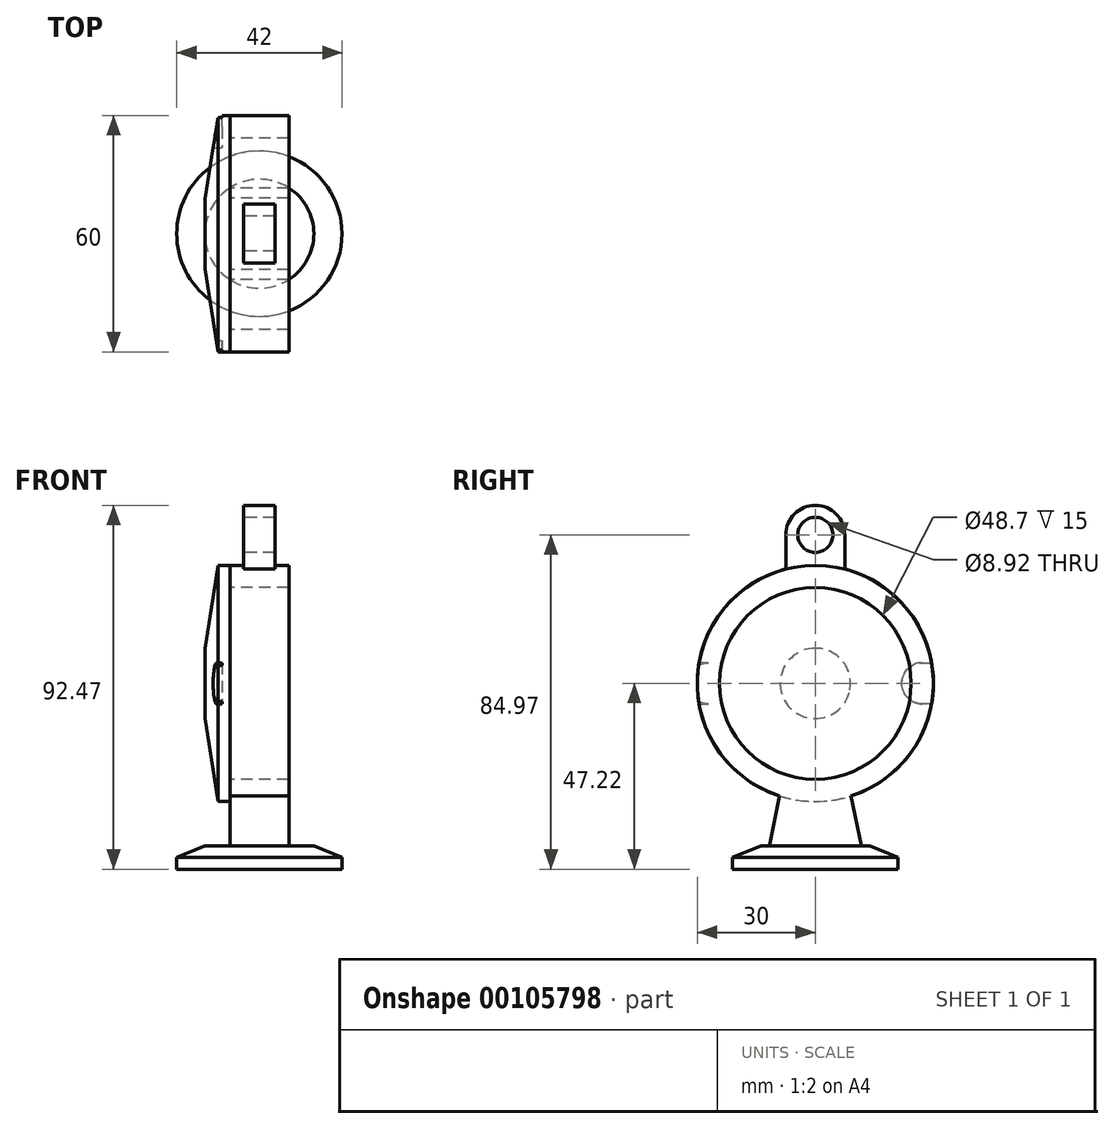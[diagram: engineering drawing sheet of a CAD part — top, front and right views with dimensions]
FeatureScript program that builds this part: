
annotation { "Feature Type Name" : "Feature", "Feature Type Description" : "" }
export const myFeature = defineFeature(function(context is Context, id is Id, definition is map)
    precondition{}
    {
        {
            var Q0;
            Q0=qCreatedBy(makeId("Right.planeOp"),FACE);
            var sketch = newSketch(context, id + "F0", { "sketchPlane" : qUnion([Q0])});
            skCircle(sketch, "E0", {"center": v(0, 0) * mm, "radius": 30 * mm});
            skArc(sketch, "E1", {"start": v(7.5, 37.75) * mm, "mid": v(0, 45.25) * mm, "end": v(-7.5, 37.75) * mm});
            skLineSegment(sketch, "E2", {"start": v(7.5, 37.75) * mm, "end": v(7.5, 29.05) * mm});
            skLineSegment(sketch, "E3", {"start": v(-7.5, 37.75) * mm, "end": v(-7.5, 29.05) * mm});
            skCircle(sketch, "E4", {"center": v(0, 0) * mm, "radius": 24.35 * mm});
            skCircle(sketch, "E5", {"center": v(0, 37.75) * mm, "radius": 4.46 * mm});
            skLineSegment(sketch, "E6", {"start": v(0, 46.89) * mm, "end": v(0, -52.68) * mm, "construction": true});
            skLineSegment(sketch, "E7", {"start": v(9.09, -28.6) * mm, "end": v(11.66, -41.22) * mm});
            skLineSegment(sketch, "E8.MirrorCS", {"start": v(-9.09, -28.6) * mm, "end": v(-11.66, -41.22) * mm});
            skLineSegment(sketch, "E9", {"start": v(11.66, -41.22) * mm, "end": v(-11.66, -41.22) * mm});
            skSolve(sketch);
        }
        {
            var Q0;
            Q0=makeQuery(id+"F0.imprint","IMPRINT",FACE,{"disambiguationData":[TD([[makeQuery(id+"F0.imprint","IMPRINT",EDGE,{"derivedFrom":sQuery(id+"F0.wireOp",EDGE,"E4")}),-1.0]])]});
            var Q1;
            {var subQ0=sQuery(id+"F0.wireOp",EDGE,"E7");Q1=makeQuery(id+"F0.imprint","IMPRINT",FACE,{"disambiguationData":[TD([[makeQuery(id+"F0.imprint","IMPRINT",EDGE,{"derivedFrom":subQ0}),-1.0]])]});}
            extrude(context, id + "F1", {"entities" : qUnion([Q0, Q1]), "endBound" : BoundingType.SYMMETRIC, "depth" : 15 * mm});
        }
        {
            var Q0;
            Q0=makeQuery(id+"F0.imprint","IMPRINT",FACE,{"disambiguationData":[TD([[makeQuery(id+"F0.imprint","IMPRINT",EDGE,{"derivedFrom":sQuery(id+"F0.wireOp",EDGE,"E1")}),1.0]])]});
            extrude(context, id + "F2", {"entities" : qUnion([Q0]), "operationType" : NewBodyOperationType.ADD, "endBound" : BoundingType.SYMMETRIC, "depth" : 8 * mm});
        }
        {
            var Q0;
            Q0=makeQuery(id+"F1.opExtrude","CAP_FACE",FACE,{"disambiguationData":[OSD([sQuery(id+"F0.wireOp",EDGE,"E0"),sQuery(id+"F0.wireOp",EDGE,"E4")])],"isStart":true});
            var sketch = newSketch(context, id + "F3", { "sketchPlane" : qUnion([Q0])});
            skLineSegment(sketch, "E10", {"start": v(0, -30) * mm, "end": v(0, 0) * mm});
            skSolve(sketch);
        }
        {
            var Q0;
            Q0=makeQuery(id+"F1.opExtrude","SWEPT_FACE",FACE,{"disambiguationData":[OSD([sQuery(id+"F0.wireOp",EDGE,"E9")])]});
            var sketch = newSketch(context, id + "F4", { "sketchPlane" : qUnion([Q0])});
            skCircle(sketch, "E11", {"center": v(0, 0) * mm, "radius": 13.86 * mm, "construction": true});
            skSolve(sketch);
        }
        {
            var Q0;
            Q0=qCreatedBy(makeId("Front.planeOp"),FACE);
            var sketch = newSketch(context, id + "F5", { "sketchPlane" : qUnion([Q0])});
            skLineSegment(sketch, "E12", {"start": v(-10.5, -30) * mm, "end": v(-13.75, -8.94) * mm});
            skLineSegment(sketch, "E13", {"start": v(-13.75, -8.94) * mm, "end": v(-13.75, 0) * mm});
            skLineSegment(sketch, "E14", {"start": v(-13.75, 0) * mm, "end": v(-7.5, 0) * mm});
            skLineSegment(sketch, "E15", {"start": v(-10.5, -30) * mm, "end": v(-7.5, -30) * mm});
            skLineSegment(sketch, "E16", {"start": v(-7.5, 0) * mm, "end": v(-7.5, -30) * mm});
            skLineSegment(sketch, "E17", {"start": v(-13.84, -41.22) * mm, "end": v(-21, -44.22) * mm});
            skLineSegment(sketch, "E18", {"start": v(-21, -44.22) * mm, "end": v(-21, -47.22) * mm});
            skLineSegment(sketch, "E19", {"start": v(-21, -47.22) * mm, "end": v(0, -47.22) * mm});
            skLineSegment(sketch, "E20", {"start": v(0, -47.22) * mm, "end": v(0, -41.22) * mm});
            skLineSegment(sketch, "E21", {"start": v(0, -41.22) * mm, "end": v(-13.84, -41.22) * mm});
            skSolve(sketch);
        }
        {
            var Q0;
            Q0=makeQuery(id+"F5.imprint","IMPRINT",FACE,{"disambiguationData":[TD([[makeQuery(id+"F5.imprint","IMPRINT",EDGE,{"derivedFrom":sQuery(id+"F5.wireOp",EDGE,"E12")}),-1.0]])]});
            var Q1;
            Q1=sQuery(id+"F5.wireOp",EDGE,"E14");
            revolve(context, id + "F6", {"entities" : qUnion([Q0]), "axis" : qUnion([Q1]), "revolveType" : RevolveType.FULL});
        }
        {
            var Q0;
            Q0=makeQuery(id+"F3.imprint","IMPRINT",FACE,{"disambiguationData":[TD([[makeQuery(id+"F3.imprint","IMPRINT",EDGE,{"derivedFrom":makeQuery(id+"F1.opExtrude","CAP_EDGE",EDGE,{"disambiguationData":[OSD([sQuery(id+"F0.wireOp",EDGE,"E0")])],"isStart":true})}),-1.0]])]});
            cPlane(context, id + "F7", {"entities" : qUnion([Q0]), "cplaneType" : CPlaneType.OFFSET, "offset" : 2 * mm, "width" : 150 * mm, "height" : 150 * mm});
        }
        {
            var Q0;
            Q0=qCreatedBy(id+"F7.planeOp",FACE);
            var sketch = newSketch(context, id + "F8", { "sketchPlane" : qUnion([Q0])});
            skLineSegment(sketch, "E22", {"start": v(-50.5, 0) * mm, "end": v(44.8, 0) * mm, "construction": true});
            skCircle(sketch, "E23", {"center": v(-27.18, 0) * mm, "radius": 2.82 * mm, "construction": true});
            skCircle(sketch, "E24", {"center": v(-27.18, 0) * mm, "radius": 5.24 * mm});
            skCircle(sketch, "E25.MirrorC", {"center": v(27.18, 0) * mm, "radius": 5.24 * mm});
            skCircle(sketch, "E26.MirrorC", {"center": v(27.18, 0) * mm, "radius": 2.82 * mm, "construction": true});
            skLineSegment(sketch, "E27", {"start": v(-27.18, 5.24) * mm, "end": v(-34.89, 5.24) * mm});
            skLineSegment(sketch, "E28", {"start": v(-34.89, 5.24) * mm, "end": v(-34.89, -5.24) * mm});
            skLineSegment(sketch, "E29", {"start": v(-34.89, -5.24) * mm, "end": v(-27.18, -5.24) * mm});
            skLineSegment(sketch, "E30.MirrorCS", {"start": v(27.18, 5.24) * mm, "end": v(34.89, 5.24) * mm});
            skLineSegment(sketch, "E31.MirrorCS", {"start": v(34.89, 5.24) * mm, "end": v(34.89, -5.24) * mm});
            skLineSegment(sketch, "E32.MirrorCS", {"start": v(34.89, -5.24) * mm, "end": v(27.18, -5.24) * mm});
            skSolve(sketch);
        }
        {
            var Q0;
            Q0=makeQuery(id+"F8.imprint","IMPRINT",FACE,{"disambiguationData":[TD([[makeQuery(id+"F8.imprint","IMPRINT",EDGE,{"derivedFrom":sQuery(id+"F8.wireOp",EDGE,"E25.MirrorC")}),-1.0]])]});
            var Q1;
            Q1=makeQuery(id+"F8.imprint","IMPRINT",FACE,{"disambiguationData":[TD([[makeQuery(id+"F8.imprint","IMPRINT",EDGE,{"derivedFrom":sQuery(id+"F8.wireOp",EDGE,"E24")}),1.0]])]});
            var Q2;
            {var subQ0=sQuery(id+"F8.wireOp",EDGE,"E27");Q2=makeQuery(id+"F8.imprint","IMPRINT",FACE,{"disambiguationData":[TD([[makeQuery(id+"F8.imprint","IMPRINT",EDGE,{"derivedFrom":subQ0}),1.0]])]});}
            var Q3;
            {var subQ0=sQuery(id+"F8.wireOp",EDGE,"E30.MirrorCS");Q3=makeQuery(id+"F8.imprint","IMPRINT",FACE,{"disambiguationData":[TD([[makeQuery(id+"F8.imprint","IMPRINT",EDGE,{"derivedFrom":subQ0}),-1.0]])]});}
            extrude(context, id + "F9", {"entities" : qUnion([Q0, Q1, Q2, Q3]), "operationType" : NewBodyOperationType.REMOVE, "depth" : 25 * mm});
        }
        {
            var Q0;
            Q0=makeQuery(id+"F5.imprint","IMPRINT",FACE,{"disambiguationData":[TD([[makeQuery(id+"F5.imprint","IMPRINT",EDGE,{"derivedFrom":sQuery(id+"F5.wireOp",EDGE,"E17")}),1.0]])]});
            var Q1;
            Q1=sQuery(id+"F5.wireOp",EDGE,"E20");
            revolve(context, id + "F10", {"operationType" : NewBodyOperationType.ADD, "entities" : qUnion([Q0]), "axis" : qUnion([Q1]), "revolveType" : RevolveType.FULL});
        }
    });
